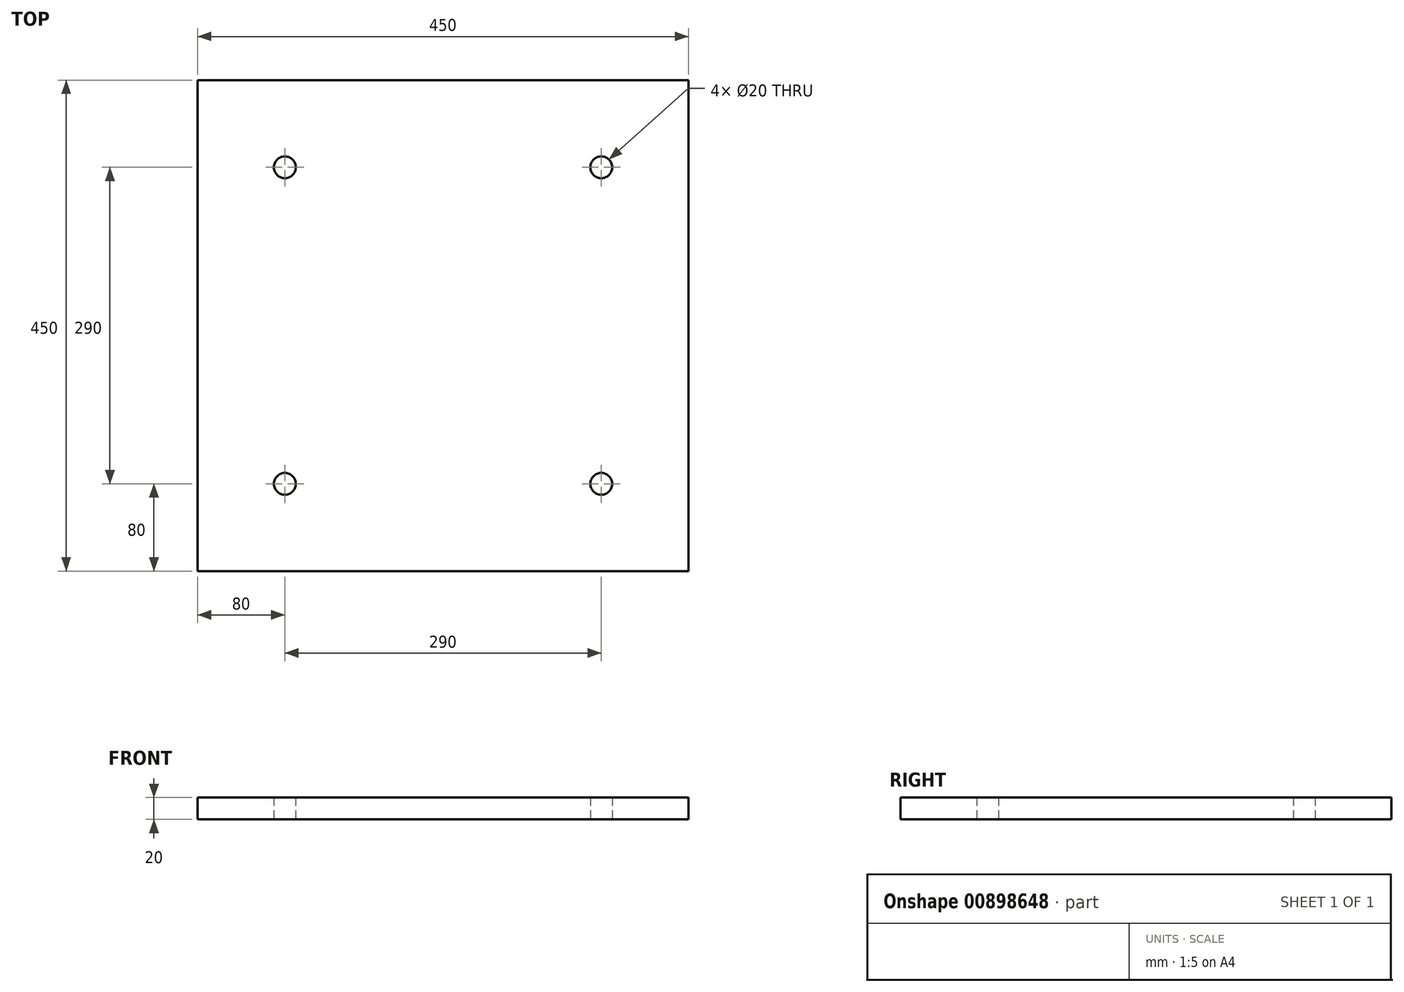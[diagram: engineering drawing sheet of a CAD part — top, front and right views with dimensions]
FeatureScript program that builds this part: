
annotation { "Feature Type Name" : "Feature", "Feature Type Description" : "" }
export const myFeature = defineFeature(function(context is Context, id is Id, definition is map)
    precondition{}
    {
        {
            var Q0;
            Q0=qCreatedBy(makeId("Top.planeOp"),FACE);
            var sketch = newSketch(context, id + "F0", { "sketchPlane" : qUnion([Q0])});
            skLineSegment(sketch, "E0.bottom", {"start": v(225, 225) * mm, "end": v(-225, 225) * mm});
            skLineSegment(sketch, "E0.top", {"start": v(225, -225) * mm, "end": v(-225, -225) * mm});
            skLineSegment(sketch, "E0.left", {"start": v(225, 225) * mm, "end": v(225, -225) * mm});
            skLineSegment(sketch, "E0.right", {"start": v(-225, 225) * mm, "end": v(-225, -225) * mm});
            skPoint(sketch, "E0.middle", {"position": v(0, 0) * mm});
            skCircle(sketch, "E1", {"center": v(-145, 145) * mm, "radius": 10 * mm});
            skCircle(sketch, "E2", {"center": v(145, 145) * mm, "radius": 10 * mm});
            skCircle(sketch, "E3", {"center": v(-145, -145) * mm, "radius": 10 * mm});
            skCircle(sketch, "E4", {"center": v(145, -145) * mm, "radius": 10 * mm});
            skSolve(sketch);
        }
        {
            var Q0;
            Q0=makeQuery(id+"F0.imprint","IMPRINT",FACE,{"disambiguationData":[TD([[makeQuery(id+"F0.imprint","IMPRINT",EDGE,{"derivedFrom":sQuery(id+"F0.wireOp",EDGE,"E0.bottom")}),1.0]])]});
            extrude(context, id + "F1", {"entities" : qUnion([Q0]), "depth" : 20 * mm, "offsetDistance" : 25 * mm});
        }
    });
